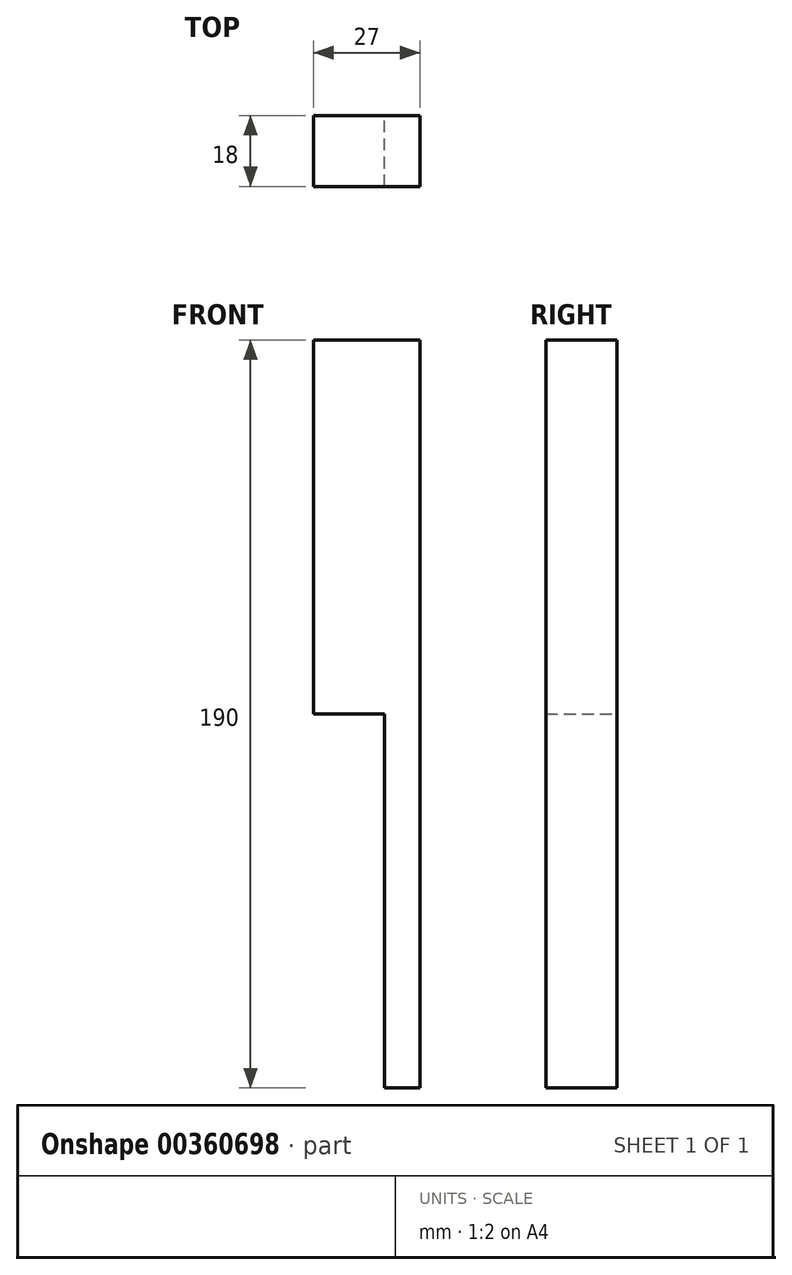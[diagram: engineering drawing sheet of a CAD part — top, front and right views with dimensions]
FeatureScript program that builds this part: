
annotation { "Feature Type Name" : "Feature", "Feature Type Description" : "" }
export const myFeature = defineFeature(function(context is Context, id is Id, definition is map)
    precondition{}
    {
        {
            var Q0;
            Q0=qCreatedBy(makeId("Front.planeOp"),FACE);
            var sketch = newSketch(context, id + "F0", { "sketchPlane" : qUnion([Q0])});
            skLineSegment(sketch, "E0.bottom", {"start": v(18, 0) * mm, "end": v(27, 0) * mm});
            skLineSegment(sketch, "E0.top", {"start": v(0, 190) * mm, "end": v(27, 190) * mm});
            skLineSegment(sketch, "E0.left", {"start": v(0, 95) * mm, "end": v(0, 190) * mm});
            skLineSegment(sketch, "E0.right", {"start": v(27, 0) * mm, "end": v(27, 190) * mm});
            skLineSegment(sketch, "E1.top", {"start": v(0, 95) * mm, "end": v(18, 95) * mm});
            skLineSegment(sketch, "E1.right", {"start": v(18, 0) * mm, "end": v(18, 95) * mm});
            skSolve(sketch);
        }
        {
            var Q0;
            Q0=makeQuery(id+"F0.imprint","IMPRINT",FACE,{"disambiguationData":[TD([[makeQuery(id+"F0.imprint","IMPRINT",EDGE,{"derivedFrom":sQuery(id+"F0.wireOp",EDGE,"E0.bottom")}),1.0]])]});
            extrude(context, id + "F1", {"entities" : qUnion([Q0]), "depth" : 18 * mm});
        }
    });
